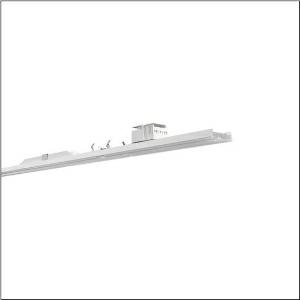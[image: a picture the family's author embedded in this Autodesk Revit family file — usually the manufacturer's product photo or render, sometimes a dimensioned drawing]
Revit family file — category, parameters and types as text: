
# Revit family: licross_r__11_recessed_mo_51tl19dv4b5f_21a5
name_source: partatom
category: Lighting Fixtures
units: mm (PartAtom-declared; Revit-internal decimal feet)

## family parameters
Cut with Voids When Loaded = No
Host = Face
Light Source = No
Part Type = Normal
Room Calculation Point = No
Round Connector Dimension = Use Diameter
Shared = No

## types (1)
- --- (1 x LED, 11510 lm, 67.8 W, 4000K)
    Apparent Load = 68 VA
    CIE Flux Codes = 55 90 98 100 100
    Color Rendering = 80
    Color Temperature = 4000K
    Default Elevation = 1800 mm
    Description = Licross® 11 Recessed MOluminaire insert, length: 2.250mm, width: 66mm, height: 67mm, LED rated luminous flux: 11.510lm, light colour: 840, control gear: DALI 2, control gear: ECG DALI, with plug, 5-pole, with phase selection, mains connection: 220..240V, AC, 50/60Hz, halogen-free wiring, primary light control with lens, of plastic, primary optical cover: cover, of PMMA, light emission: direct distribution, primary light characteristic: double asymmetric, protection rating (complete): IP40, insulation class (complete): insulation class I (protective earthing), certification: CE, ENEC, VDE, protection symbol: D if used in an environment without relevant dust loads with corresponding accessories, permissible ambient temperature for indoor applications: -25..+40°C, corresponds to IFS (International Featured Standards) requirements for safety and quality in the food industry, reducing of maximum allowable ambient temperature of 5°C with ceiling mounting, packaging unit: 1 piece
    Height = 58 mm
    Lamp = 1 x LED
    Lamp Light Flux = 11510 lm
    Lamp Power = 67.8 W
    Lamp count = 1
    Length = 2250 mm
    Luminous efficacy = 170 lm/W
    Manufacturer = Siteco
    ModVariant = No
    Model = 51TL19DV4B5F
    Mounting Place = Ceiling
    Mounting Type = Pendant
    Number of Poles = 1
    OnlyDefault = Yes
    Power Factor = 1
    Product Name = Licross® 11 Recessed MO
    Product group = luminaire insert
    ProductGroupID = 902
    Protection Class = Protection class I
    Protection Degree = IP 40
    RLX_Detail_Level = 1
    RlxData = <blob elided: 27441 chars, md5=54bfa844>
    Socket = socket
    Standby Power = 0 W
    System Light Flux = 11510 lm
    System Power = 68 W
    Type Comments = factory setting: luminous flux: 100 % | dim-lin: 254 | 305 mA
    Type Image = l_1266722.jpg
    URL = http://relux.com
    VarID = @adj_133330
    Voltage = 0 V
    Weight = 0.00 kg
    Width = 66 mm

## geometry (parser evidence)
native form markers: Blend x4, Sweep x9
no freeform markers — native parametric forms only
